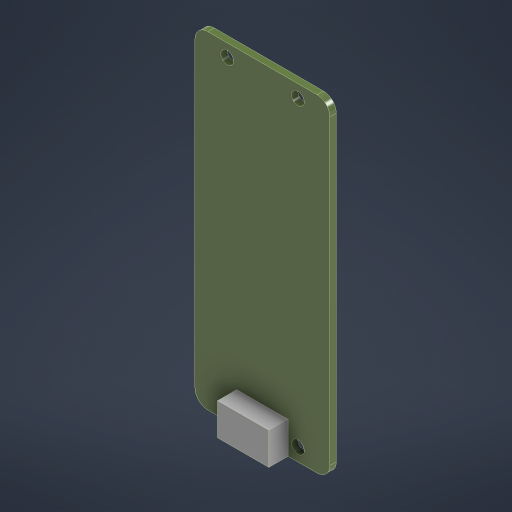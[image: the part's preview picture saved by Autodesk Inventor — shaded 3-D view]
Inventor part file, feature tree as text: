
AUTODESK INVENTOR PART (.ipt)
format: ipt  version: 2023.2 (Build 272271000, 271)  size: 242,176 bytes
history: native  units: mm
features: sketch x2, other x1
ambient origin geometry x8: Origin, YZ Plane, XZ Plane, XY Plane, X Axis, Y Axis, Z Axis, Center Point
bodies: Body1 (feature_tree), Body2 (feature_tree)
feature tree (3):
  sketch  "Sketch1"  dims[d228=21.0mm]
  sketch  "Sketch3"  dims[d229=51.0mm d230=1.0mm d231=0.0mm d233=2.0mm d234=2.0mm d235=5.0mm d236=2.0mm d240=1.0mm d241=0.0mm d242=8.0mm d243=5.0mm d244=4.5mm d245=3.0mm d246=0.0mm d9=0.5mm d10=0.872665mm d11=0.5mm d12=0.872665mm d13=0.5mm d14=0.872665mm d27=0.5mm d28=0.872665mm d29=0.5mm d30=0.872665mm d88=0.5mm d89=0.872665mm d90=0.5mm d91=0.872665mm d116=0.5mm d117=0.872665mm d118=0.5mm d119=0.872665mm d154=0.5mm d155=0.872665mm d156=0.5mm d157=0.872665mm d181=0.5mm d182=0.872665mm d183=0.5mm d184=0.872665mm d221=0.5mm d222=0.872665mm d223=0.5mm d224=0.872665mm]
  other  "USB"
